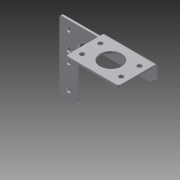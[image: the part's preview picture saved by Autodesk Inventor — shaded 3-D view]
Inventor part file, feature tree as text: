
AUTODESK INVENTOR PART (.ipt)
format: ipt  version: 2014 SP1 (Build 180222100, 222)  size: 232,448 bytes
history: native  units: in
note: dims shown in document units (in); Inventor stores cm internally (conversion verified against a paired STEP export)
features: other x4, sheet_metal_op x3, sketch x3, chamfer x1
ambient origin geometry x8: Origin, YZ Plane, XZ Plane, XY Plane, X Axis, Y Axis, Z Axis, Center Point
bodies: Solid1 (feature_tree)
feature tree (11):
  sheet_metal_op  "Face1"
  sheet_metal_op  "Flange1"
  chamfer  "Corner Round1"
  sketch  "Sketch1"  dims[d0=1.0in]
  other  "Plate1"
  sketch  "Sketch2"  dims[d2=0.26in]
  other  "Plate2"
  sheet_metal_op  "Bend1"
  sketch  "Sketch3"  dims[d3=0.26in d4=2.0in d5=1.0in d6=4.5in d7=0.75in d8=3.0in d9=0.125in d10=0.12in d11=0.12in d12=0.06in d13=0.24in d14=0.12in d15=2.25in d16=90.0deg d17=0.05in d18=0.48in d19=0.12in d20=0.12in d21=0.5in d22=0.125in d23=0.26in d25=0.375in d26=0.5in d27=0.12in d28=0.0in d29=0.53in d30=0.395in d31=1.25in d32=2.0in d33=0.26in d34=0.5in d35=1.378in d1=0.0625in]
  other  "Cut1"
  other  "Definition1"
